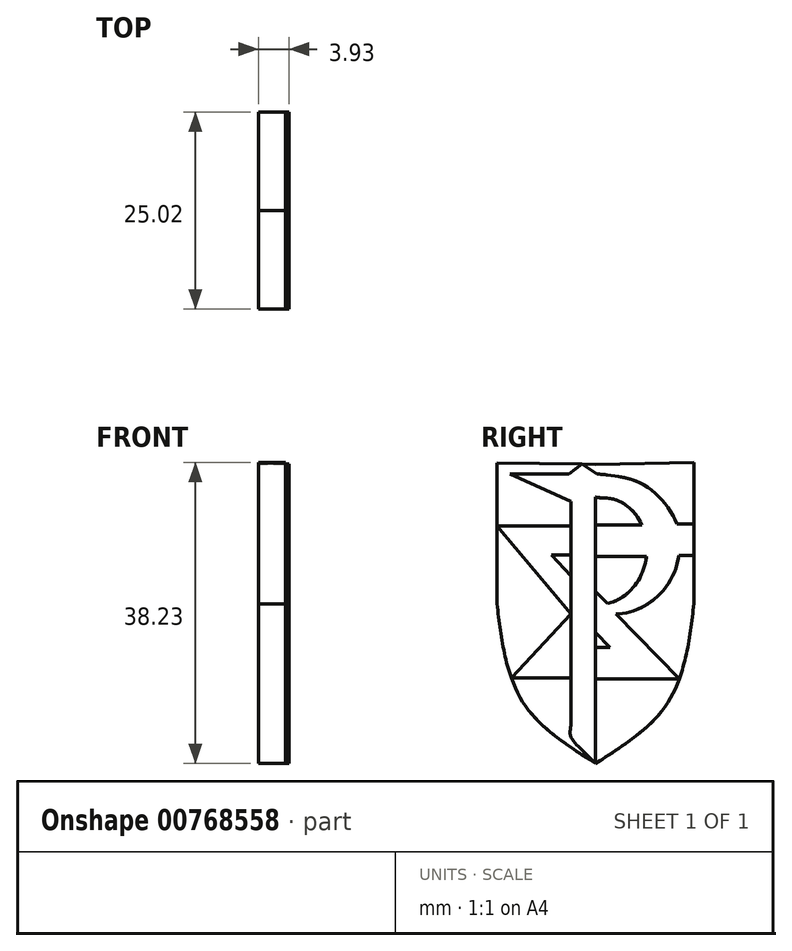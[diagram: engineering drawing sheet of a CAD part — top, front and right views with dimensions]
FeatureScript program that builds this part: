
annotation { "Feature Type Name" : "Feature", "Feature Type Description" : "" }
export const myFeature = defineFeature(function(context is Context, id is Id, definition is map)
    precondition{}
    {
        {
            var Q0;
            Q0=qCreatedBy(makeId("Right.planeOp"),FACE);
            var sketch = newSketch(context, id + "F0", { "sketchPlane" : qUnion([Q0])});
            skLineSegment(sketch, "E0.right", {"start": v(-12.53, 2.17) * mm, "end": v(-12.54, 20.07) * mm});
            skLineSegment(sketch, "E1", {"start": v(-0.04, 19.87) * mm, "end": v(0, -18.13) * mm, "construction": true});
            skLineSegment(sketch, "E2", {"start": v(-12.54, 20.07) * mm, "end": v(-0.04, 19.87) * mm});
            skFitSpline(sketch, "E3", {"points": [v(-12.53, 2.17) * mm, v(-9.22, -10.36) * mm, v(0, -18.13) * mm], "startDerivative": vector(3.03, -26.41) * mm, "endDerivative": vector(21.7, -13.98) * mm});
            skLineSegment(sketch, "E4.MirrorCS", {"start": v(12.46, 20.1) * mm, "end": v(-0.04, 19.87) * mm});
            skLineSegment(sketch, "E5.MirrorCS", {"start": v(12.48, 2.2) * mm, "end": v(12.46, 20.1) * mm});
            skFitSpline(sketch, "E6.MirrorCS", {"points": [v(12.48, 2.2) * mm, v(9.2, -10.34) * mm, v(0, -18.13) * mm], "startDerivative": vector(-2.97, -26.42) * mm, "endDerivative": vector(-21.66, -14.03) * mm});
            skSolve(sketch);
        }
        {
            var Q0;
            Q0=qSketchRegion(id+"F0",true);
            extrude(context, id + "F1", {"entities" : qUnion([Q0]), "depth" : 3.46 * mm, "offsetDistance" : 25 * mm});
        }
        {
            var Q0;
            Q0=makeQuery(id+"F1.opExtrude","CAP_FACE",FACE,{"disambiguationData":[OSD([sQuery(id+"F0.wireOp",EDGE,"E0.right"),sQuery(id+"F0.wireOp",EDGE,"E2"),sQuery(id+"F0.wireOp",EDGE,"E3"),sQuery(id+"F0.wireOp",EDGE,"E4.MirrorCS"),sQuery(id+"F0.wireOp",EDGE,"E5.MirrorCS"),sQuery(id+"F0.wireOp",EDGE,"E6.MirrorCS")])],"isStart":false});
            var sketch = newSketch(context, id + "F2", { "sketchPlane" : qUnion([Q0])});
            skFitSpline(sketch, "E7", {"points": [v(0, -18.13) * mm, v(-1.77, -16.4) * mm, v(-3.2, -14.53) * mm, v(-3.14, -12.8) * mm], "startDerivative": vector(-5, 4.79) * mm, "endDerivative": vector(-0.47, 5.86) * mm});
            skLineSegment(sketch, "E8", {"start": v(-3.14, -12.8) * mm, "end": v(-3.14, 15.14) * mm});
            skFitSpline(sketch, "E9", {"points": [v(0, 15.71) * mm, v(2.05, 15.5) * mm, v(4.66, 13.98) * mm, v(6.52, 9.69) * mm, v(5.14, 4.7) * mm, v(2.05, 2.35) * mm, v(0.17, 1.85) * mm], "startDerivative": vector(18.85, -4.03) * mm, "endDerivative": vector(-7.6, -4.54) * mm});
            skFitSpline(sketch, "E10", {"points": [v(0.17, 1.85) * mm, v(1.8, 0.97) * mm, v(5.72, 1.64) * mm, v(9.74, 5.6) * mm, v(10.56, 11.42) * mm, v(8.68, 15.03) * mm, v(5.69, 17.5) * mm, v(2.3, 18.42) * mm, v(0.17, 18.64) * mm], "startDerivative": vector(16.34, -11.7) * mm, "endDerivative": vector(-21.6, 0.97) * mm});
            skLineSegment(sketch, "E11", {"start": v(0.17, 18.64) * mm, "end": v(-1.75, 19.9) * mm});
            skLineSegment(sketch, "E12", {"start": v(-1.75, 19.9) * mm, "end": v(-3.36, 18.64) * mm});
            skLineSegment(sketch, "E13", {"start": v(-3.36, 18.64) * mm, "end": v(-10.88, 18.64) * mm});
            skLineSegment(sketch, "E14", {"start": v(-10.88, 18.64) * mm, "end": v(-3.14, 15.14) * mm});
            skLineSegment(sketch, "E15", {"start": v(0, 15.71) * mm, "end": v(0, -18.13) * mm});
            skSolve(sketch);
        }
        {
            var Q0;
            Q0=qSketchRegion(id+"F2",true);
            extrude(context, id + "F3", {"entities" : qUnion([Q0]), "operationType" : NewBodyOperationType.ADD, "depth" : 0.47 * mm, "offsetDistance" : 25 * mm});
        }
        {
            var Q0;
            {var subQ0=sQuery(id+"F0.wireOp",EDGE,"E3");var subQ1=sQuery(id+"F0.wireOp",EDGE,"E6.MirrorCS");var subQ2=sQuery(id+"F0.wireOp",EDGE,"E5.MirrorCS");var subQ3=sQuery(id+"F0.wireOp",EDGE,"E4.MirrorCS");var subQ4=sQuery(id+"F0.wireOp",EDGE,"E2");var subQ5=makeQuery(id+"F1.opExtrude","CAP_FACE",FACE,{"disambiguationData":[OSD([sQuery(id+"F0.wireOp",EDGE,"E0.right"),subQ4,subQ0,subQ3,subQ2,subQ1])],"isStart":false});Q0=makeQuery(id+"F3.boolean.opBoolean","SPLIT",FACE,{"disambiguationData":[TD([makeQuery(id+"F1.opExtrude","SWEPT_FACE",FACE,{"disambiguationData":[OSD([subQ3])]})])],"derivedFrom":subQ5});}
            var sketch = newSketch(context, id + "F4", { "sketchPlane" : qUnion([Q0])});
            skPoint(sketch, "E16.end.orphan", {"position": v(0, 8.16) * mm});
            skPoint(sketch, "E17", {"position": v(0, 12.16) * mm});
            skLineSegment(sketch, "E18", {"start": v(0, 12.16) * mm, "end": v(5.88, 12.16) * mm});
            skLineSegment(sketch, "E19", {"start": v(0, 8.16) * mm, "end": v(6.47, 8.16) * mm});
            skLineSegment(sketch, "E20", {"start": v(10.32, 12.3) * mm, "end": v(12.47, 12.3) * mm});
            skLineSegment(sketch, "E21", {"start": v(10.58, 8.3) * mm, "end": v(12.47, 8.3) * mm});
            skPoint(sketch, "E22", {"position": v(0, 3.74) * mm});
            skPoint(sketch, "E23", {"position": v(0, -7.42) * mm});
            skLineSegment(sketch, "E24", {"start": v(0, 3.74) * mm, "end": v(1.49, 2.2) * mm});
            skLineSegment(sketch, "E25", {"start": v(2.6, 0.89) * mm, "end": v(10.62, -7.42) * mm});
            skLineSegment(sketch, "E26", {"start": v(10.62, -7.42) * mm, "end": v(0, -7.42) * mm});
            skLineSegment(sketch, "E27", {"start": v(0, -1.45) * mm, "end": v(1.8, -3.42) * mm});
            skLineSegment(sketch, "E28", {"start": v(1.8, -3.42) * mm, "end": v(0, -3.42) * mm});
            skLineSegment(sketch, "E29", {"start": v(-12.54, 12.11) * mm, "end": v(-3.14, 12.11) * mm});
            skLineSegment(sketch, "E30", {"start": v(0, -1.45) * mm, "end": v(-8.87, 8.21) * mm, "construction": true});
            skPoint(sketch, "E31.startSnap0", {"position": v(-4.44, 3.38) * mm});
            skLineSegment(sketch, "E32", {"start": v(0, 3.74) * mm, "end": v(-4.3, 8.21) * mm, "construction": true});
            skLineSegment(sketch, "E33", {"start": v(-3.15, 7.02) * mm, "end": v(-4.3, 8.21) * mm});
            skLineSegment(sketch, "E34", {"start": v(-3.14, 1.96) * mm, "end": v(-8.87, 8.21) * mm});
            skLineSegment(sketch, "E35", {"start": v(-3.14, 1.96) * mm, "end": v(-10.67, -7.24) * mm, "construction": true});
            skLineSegment(sketch, "E36", {"start": v(-10.67, -7.24) * mm, "end": v(0, -7.42) * mm, "construction": true});
            skLineSegment(sketch, "E37", {"start": v(-3.14, 1.96) * mm, "end": v(-10.67, -7.24) * mm});
            skLineSegment(sketch, "E38", {"start": v(-3.14, -7.36) * mm, "end": v(-10.67, -7.24) * mm});
            skLineSegment(sketch, "E39", {"start": v(-8.87, 8.21) * mm, "end": v(-12.54, 12.11) * mm});
            skLineSegment(sketch, "E40", {"start": v(0, 8.16) * mm, "end": v(-4.3, 8.21) * mm, "construction": true});
            skLineSegment(sketch, "E41", {"start": v(-3.14, 8.2) * mm, "end": v(-4.3, 8.21) * mm});
            skSolve(sketch);
        }
        {
            var Q0;
            {var subQ0=sQuery(id+"F4.wireOp",EDGE,"E18");Q0=makeQuery(id+"F4.imprint","IMPRINT",FACE,{"disambiguationData":[TD([[makeQuery(id+"F4.imprint","IMPRINT",EDGE,{"derivedFrom":subQ0}),-1.0]])]});}
            var Q1;
            {var subQ0=sQuery(id+"F4.wireOp",EDGE,"E20");Q1=makeQuery(id+"F4.imprint","IMPRINT",FACE,{"disambiguationData":[TD([[makeQuery(id+"F4.imprint","IMPRINT",EDGE,{"derivedFrom":subQ0}),-1.0]])]});}
            var Q2;
            {var subQ4=sQuery(id+"F4.wireOp",EDGE,"E24");Q2=makeQuery(id+"F4.imprint","IMPRINT",FACE,{"disambiguationData":[TD([[makeQuery(id+"F4.imprint","IMPRINT",EDGE,{"derivedFrom":subQ4}),-1.0]])]});}
            extrude(context, id + "F5", {"entities" : qUnion([Q0, Q1, Q2]), "operationType" : NewBodyOperationType.ADD, "depth" : 0.46 * mm, "offsetDistance" : 25 * mm});
        }
        {
            var Q0;
            {var subQ0=sQuery(id+"F0.wireOp",EDGE,"E3");var subQ1=sQuery(id+"F0.wireOp",EDGE,"E6.MirrorCS");var subQ2=sQuery(id+"F0.wireOp",EDGE,"E0.right");var subQ3=sQuery(id+"F0.wireOp",EDGE,"E2");var subQ4=makeQuery(id+"F1.opExtrude","CAP_FACE",FACE,{"disambiguationData":[OSD([subQ2,subQ3,subQ0,sQuery(id+"F0.wireOp",EDGE,"E4.MirrorCS"),sQuery(id+"F0.wireOp",EDGE,"E5.MirrorCS"),subQ1])],"isStart":false});Q0=makeQuery(id+"F3.boolean.opBoolean","SPLIT",FACE,{"disambiguationData":[TD([makeQuery(id+"F1.opExtrude","SWEPT_FACE",FACE,{"disambiguationData":[OSD([subQ2])]})])],"derivedFrom":subQ4});}
            var sketch = newSketch(context, id + "F6", { "sketchPlane" : qUnion([Q0])});
            skLineSegment(sketch, "E42", {"start": v(-3.14, -7.26) * mm, "end": v(-10.7, -7.26) * mm});
            skLineSegment(sketch, "E43", {"start": v(-10.7, -7.26) * mm, "end": v(-3.14, 0.87) * mm});
            skLineSegment(sketch, "E44", {"start": v(-3.14, 0.87) * mm, "end": v(-12.54, 12.04) * mm});
            skLineSegment(sketch, "E45", {"start": v(-3.14, 12.04) * mm, "end": v(-12.54, 12.04) * mm});
            skLineSegment(sketch, "E46", {"start": v(-3.14, 5.7) * mm, "end": v(-5.62, 8.37) * mm});
            skLineSegment(sketch, "E47", {"start": v(-5.62, 8.37) * mm, "end": v(-3.14, 8.37) * mm});
            skSolve(sketch);
        }
        {
            var Q0;
            Q0=qSketchRegion(id+"F6",true);
            var Q1;
            {var subQ3=sQuery(id+"F6.wireOp",EDGE,"E44");Q1=makeQuery(id+"F6.imprint","IMPRINT",FACE,{"disambiguationData":[TD([[makeQuery(id+"F6.imprint","IMPRINT",EDGE,{"derivedFrom":subQ3}),-1.0]])]});}
            var Q2;
            {var subQ0=sQuery(id+"F6.wireOp",EDGE,"E42");Q2=makeQuery(id+"F6.imprint","IMPRINT",FACE,{"disambiguationData":[TD([[makeQuery(id+"F6.imprint","IMPRINT",EDGE,{"derivedFrom":subQ0}),-1.0]])]});}
            extrude(context, id + "F7", {"entities" : qUnion([Q0, Q1, Q2]), "operationType" : NewBodyOperationType.ADD, "depth" : 0.46 * mm, "offsetDistance" : 25 * mm});
        }
    });
